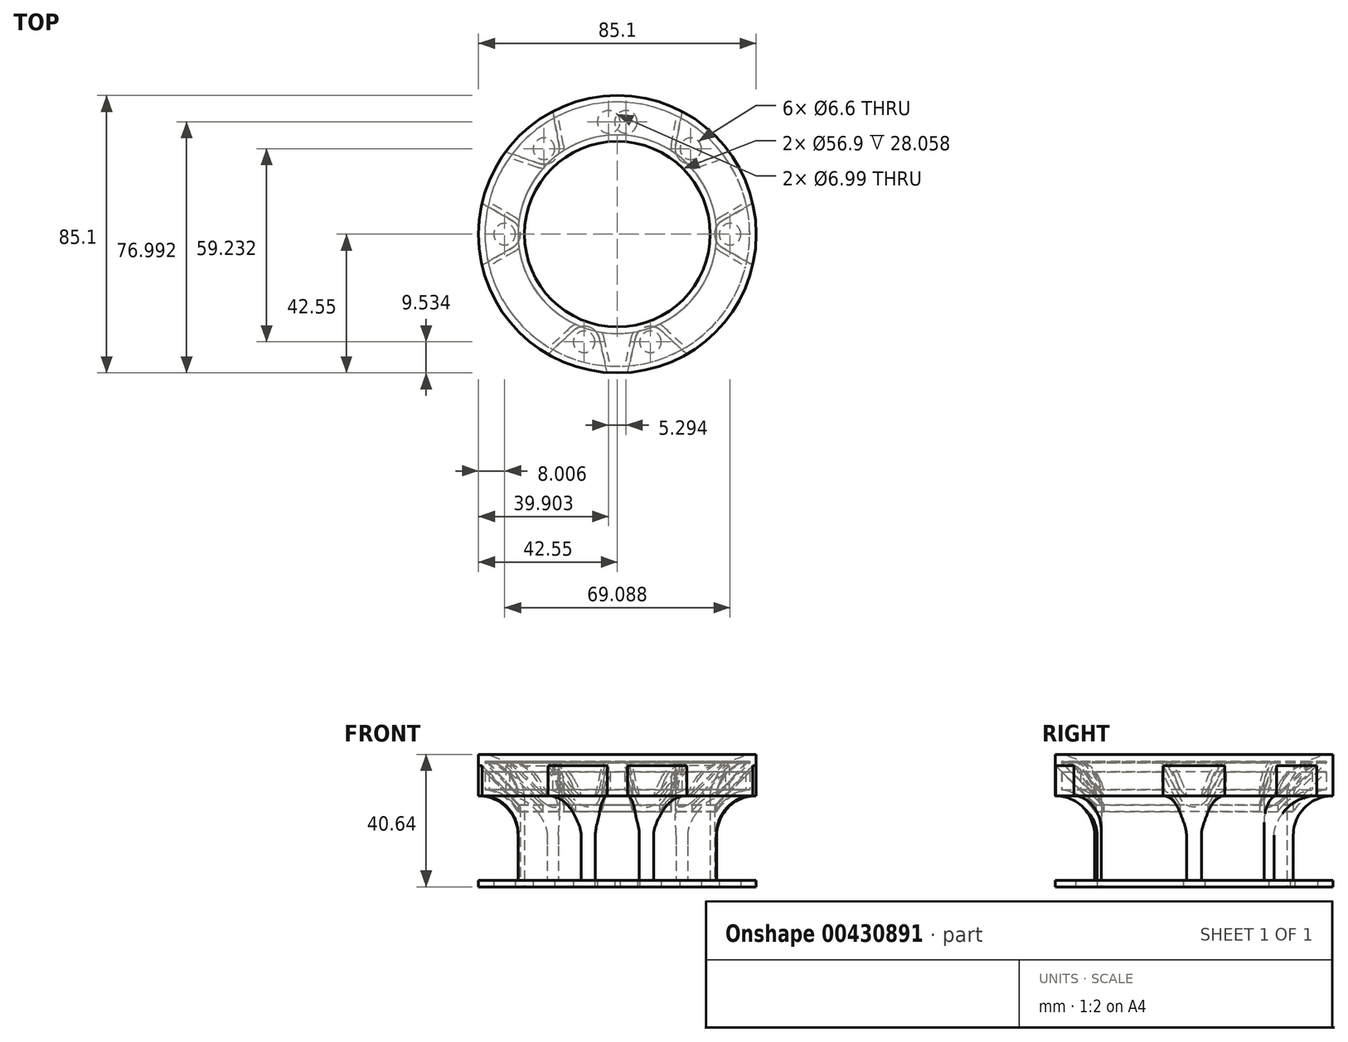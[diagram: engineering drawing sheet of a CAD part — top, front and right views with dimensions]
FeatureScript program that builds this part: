
annotation { "Feature Type Name" : "Feature", "Feature Type Description" : "" }
export const myFeature = defineFeature(function(context is Context, id is Id, definition is map)
    precondition{}
    {
        {
            var Q0;
            Q0=qCreatedBy(makeId("Front.planeOp"),FACE);
            var sketch = newSketch(context, id + "F0", { "sketchPlane" : qUnion([Q0])});
            skLineSegment(sketch, "E0", {"start": v(-42.55, 0) * mm, "end": v(-28.45, 0) * mm});
            skLineSegment(sketch, "E1", {"start": v(-28.45, 0) * mm, "end": v(-28.45, 28.06) * mm});
            skLineSegment(sketch, "E2", {"start": v(-42.55, 40.64) * mm, "end": v(-42.55, 27.94) * mm});
            skArc(sketch, "E3", {"start": v(-42.55, 40.64) * mm, "mid": v(-33.1, 37.04) * mm, "end": v(-28.45, 28.06) * mm});
            skArc(sketch, "E4.0", {"start": v(-40.55, 38.47) * mm, "mid": v(-33.75, 34.89) * mm, "end": v(-30.45, 27.94) * mm});
            skLineSegment(sketch, "E5.0", {"start": v(-42.55, 2) * mm, "end": v(-30.45, 2) * mm});
            skLineSegment(sketch, "E6.0", {"start": v(-30.45, 2) * mm, "end": v(-30.45, 15.84) * mm});
            skLineSegment(sketch, "E7", {"start": v(-42.55, 2) * mm, "end": v(-42.55, 0) * mm});
            skLineSegment(sketch, "E8.trimOffspring", {"start": v(-40.55, 38.47) * mm, "end": v(-40.55, 38.04) * mm});
            skLineSegment(sketch, "E9.trimOffspring", {"start": v(-30.45, 23.08) * mm, "end": v(-30.45, 25.11) * mm});
            skLineSegment(sketch, "E10", {"start": v(-30.45, 27.94) * mm, "end": v(-40.55, 38.04) * mm});
            skLineSegment(sketch, "E11.0", {"start": v(-30.45, 25.11) * mm, "end": v(-40.55, 35.2) * mm});
            skLineSegment(sketch, "E12.trimOffspring", {"start": v(-40.55, 35.2) * mm, "end": v(-40.55, 29.8) * mm});
            skArc(sketch, "E13", {"start": v(-30.45, 15.84) * mm, "mid": v(-34, 24.4) * mm, "end": v(-42.55, 27.94) * mm});
            skArc(sketch, "E14.0", {"start": v(-30.45, 23.08) * mm, "mid": v(-34.74, 27.58) * mm, "end": v(-40.55, 29.8) * mm});
            skSolve(sketch);
        }
        {
            var Q0;
            Q0=qCreatedBy(makeId("Front.planeOp"),FACE);
            var sketch = newSketch(context, id + "F1", { "sketchPlane" : qUnion([Q0])});
            skLineSegment(sketch, "E15", {"start": v(0, 0) * mm, "end": v(0, 53.03) * mm});
            skSolve(sketch);
        }
        {
            var Q0;
            Q0=makeQuery(id+"F0.imprint","IMPRINT",FACE,{"disambiguationData":[TD([[makeQuery(id+"F0.imprint","IMPRINT",EDGE,{"derivedFrom":sQuery(id+"F0.wireOp",EDGE,"E0")}),1.0]])]});
            var Q1;
            Q1=sQuery(id+"F0.wireOp",EDGE,"E2");
            var Q2;
            Q2=sQuery(id+"F0.wireOp",EDGE,"E3");
            var Q3;
            Q3=sQuery(id+"F0.wireOp",EDGE,"E1");
            var Q4;
            Q4=sQuery(id+"F0.wireOp",EDGE,"E0");
            var Q5;
            Q5=sQuery(id+"F1.wireOp",EDGE,"E15");
            revolve(context, id + "F2", {"entities" : qUnion([Q0]), "surfaceEntities" : qUnion([Q1, Q2, Q3, Q4]), "axis" : qUnion([Q5]), "revolveType" : RevolveType.FULL});
        }
        {
            var Q0;
            Q0=qCreatedBy(makeId("Top.planeOp"),FACE);
            var sketch = newSketch(context, id + "F3", { "sketchPlane" : qUnion([Q0])});
            skCircle(sketch, "E16", {"center": v(-34.54, 0) * mm, "radius": 3.3 * mm});
            skCircle(sketch, "E17", {"center": v(-2.65, 34.44) * mm, "radius": 3.5 * mm});
            skCircle(sketch, "E18", {"center": v(10.16, -33.02) * mm, "radius": 3.3 * mm});
            skCircle(sketch, "E19", {"center": v(22.5, 26.22) * mm, "radius": 3.3 * mm});
            skSolve(sketch);
        }
        {
            var Q0;
            Q0 = qSketchRegion(id + "F3", true);
            extrude(context, id + "F4", {"entities" : qUnion([Q0]), "operationType" : NewBodyOperationType.REMOVE, "endBound" : BoundingType.UP_TO_NEXT, "depth" : 4.06 * mm});
        }
        {
            var Q0;
            Q0=makeQuery(id+"F2.opRevolve","SWEPT_FACE",FACE,{"disambiguationData":[OSD([sQuery(id+"F0.wireOp",EDGE,"E5.0")])]});
            var sketch = newSketch(context, id + "F5", { "sketchPlane" : qUnion([Q0])});
            skArc(sketch, "E20", {"start": v(-32.16, -4.12) * mm, "mid": v(-29.78, 0) * mm, "end": v(-32.16, 4.12) * mm});
            skArc(sketch, "E21", {"start": v(17.82, 27.1) * mm, "mid": v(19.4, 22.6) * mm, "end": v(24.08, 21.72) * mm});
            skArc(sketch, "E22", {"start": v(13.4, -29.53) * mm, "mid": v(8.76, -28.46) * mm, "end": v(5.52, -31.95) * mm});
            skLineSegment(sketch, "E23", {"start": v(-32.16, 4.12) * mm, "end": v(-41.47, 9.5) * mm});
            skLineSegment(sketch, "E24", {"start": v(-32.16, -4.12) * mm, "end": v(-41.47, -9.5) * mm});
            skLineSegment(sketch, "E25", {"start": v(13.4, -29.53) * mm, "end": v(21.28, -36.84) * mm});
            skLineSegment(sketch, "E26", {"start": v(5.52, -31.95) * mm, "end": v(3.12, -42.43) * mm});
            skLineSegment(sketch, "E27", {"start": v(17.82, 27.1) * mm, "end": v(19.8, 37.66) * mm});
            skLineSegment(sketch, "E28", {"start": v(24.08, 21.72) * mm, "end": v(34.21, 25.29) * mm});
            skArc(sketch, "E29", {"start": v(-41.47, 9.5) * mm, "mid": v(-42.55, 0) * mm, "end": v(-41.47, -9.5) * mm});
            skArc(sketch, "E30.trimOffspring", {"start": v(34.21, 25.29) * mm, "mid": v(27.7, 32.29) * mm, "end": v(19.8, 37.66) * mm});
            skArc(sketch, "E31.trimOffspring", {"start": v(3.12, -42.43) * mm, "mid": v(12.51, -40.66) * mm, "end": v(21.28, -36.84) * mm});
            skLineSegment(sketch, "E32", {"start": v(-29.78, 0) * mm, "end": v(0, 0) * mm});
            skLineSegment(sketch, "E33", {"start": v(19.4, 22.6) * mm, "end": v(0, 0) * mm});
            skLineSegment(sketch, "E34", {"start": v(0, 0) * mm, "end": v(8.76, -28.46) * mm});
            skSolve(sketch);
        }
        {
            var Q0;
            Q0 = qSketchRegion(id + "F5", true);
            var Q1;
            Q1=makeQuery(id+"F2.opRevolve","SWEPT_FACE",FACE,{"disambiguationData":[OSD([sQuery(id+"F0.wireOp",EDGE,"E11.0")])]});
            var Q2;
            Q2=makeQuery(id+"FeETeO8mRZ9KAlR_1.opThicken","SWEPT_BODY",BODY,{"disambiguationData":[OSD([sQuery(id+"F0.wireOp",EDGE,"E0")])]});
            extrude(context, id + "F6", {"entities" : qUnion([Q0]), "operationType" : NewBodyOperationType.REMOVE, "endBound" : BoundingType.UP_TO_SURFACE, "endBoundEntityFace" : qUnion([Q1]), "endBoundEntityBody" : qUnion([Q2]), "depth" : 22.73 * mm, "offsetDistance" : 25 * mm});
        }
        {
            var Q0;
            Q0=qCreatedBy(makeId("Top.planeOp"),FACE);
            cPlane(context, id + "F7", {"entities" : qUnion([Q0]), "cplaneType" : CPlaneType.OFFSET, "offset" : 30 * mm, "width" : 150 * mm, "height" : 150 * mm});
        }
        {
            var Q0;
            Q0=qCreatedBy(id+"F7.planeOp",FACE);
            var sketch = newSketch(context, id + "F8", { "sketchPlane" : qUnion([Q0])});
            skArc(sketch, "E35", {"start": v(-32.16, -4.12) * mm, "mid": v(-29.78, 0) * mm, "end": v(-32.16, 4.12) * mm});
            skArc(sketch, "E36", {"start": v(17.81, 27.09) * mm, "mid": v(19.4, 22.6) * mm, "end": v(24.08, 21.72) * mm});
            skArc(sketch, "E37", {"start": v(13.4, -29.53) * mm, "mid": v(8.76, -28.46) * mm, "end": v(5.52, -31.95) * mm});
            skArc(sketch, "E38", {"start": v(-41.14, 10.85) * mm, "mid": v(-41.31, 10.17) * mm, "end": v(-41.47, 9.5) * mm});
            skLineSegment(sketch, "E39", {"start": v(-32.16, 4.12) * mm, "end": v(-41.47, 9.5) * mm});
            skLineSegment(sketch, "E40", {"start": v(-32.16, -4.12) * mm, "end": v(-41.47, -9.5) * mm});
            skLineSegment(sketch, "E41", {"start": v(13.4, -29.53) * mm, "end": v(21.28, -36.84) * mm});
            skLineSegment(sketch, "E42", {"start": v(24.08, 21.72) * mm, "end": v(34.21, 25.29) * mm});
            skLineSegment(sketch, "E43", {"start": v(17.81, 27.09) * mm, "end": v(19.8, 37.66) * mm});
            skLineSegment(sketch, "E44", {"start": v(5.52, -31.95) * mm, "end": v(3.12, -42.43) * mm});
            skLineSegment(sketch, "E45.0", {"start": v(-31.5, 5.28) * mm, "end": v(-41.14, 10.85) * mm});
            skArc(sketch, "E46.0", {"start": v(-31.5, -5.28) * mm, "mid": v(-28.45, 0) * mm, "end": v(-31.5, 5.28) * mm});
            skLineSegment(sketch, "E47.0", {"start": v(-31.5, -5.28) * mm, "end": v(-41.14, -10.85) * mm});
            skLineSegment(sketch, "E48.0", {"start": v(16.5, 27.33) * mm, "end": v(18.56, 38.28) * mm});
            skArc(sketch, "E49.0", {"start": v(16.5, 27.33) * mm, "mid": v(18.53, 21.59) * mm, "end": v(24.52, 20.47) * mm});
            skLineSegment(sketch, "E50.0", {"start": v(24.48, 20.45) * mm, "end": v(35.02, 24.16) * mm});
            skLineSegment(sketch, "E51.0", {"start": v(4.22, -31.66) * mm, "end": v(1.74, -42.5) * mm});
            skArc(sketch, "E52.0", {"start": v(14.31, -28.55) * mm, "mid": v(8.37, -27.19) * mm, "end": v(4.22, -31.66) * mm});
            skLineSegment(sketch, "E53.0", {"start": v(14.31, -28.55) * mm, "end": v(22.47, -36.13) * mm});
            skArc(sketch, "E54.trimOffspring", {"start": v(35.02, 24.16) * mm, "mid": v(34.62, 24.73) * mm, "end": v(34.21, 25.29) * mm});
            skArc(sketch, "E55.trimOffspring", {"start": v(1.74, -42.5) * mm, "mid": v(2.43, -42.48) * mm, "end": v(3.12, -42.43) * mm});
            skArc(sketch, "E56.trimOffspring", {"start": v(-41.47, -9.5) * mm, "mid": v(-41.31, -10.17) * mm, "end": v(-41.14, -10.85) * mm});
            skArc(sketch, "E57.trimOffspring", {"start": v(19.8, 37.66) * mm, "mid": v(19.18, 37.98) * mm, "end": v(18.56, 38.28) * mm});
            skArc(sketch, "E58.trimOffspring", {"start": v(21.28, -36.84) * mm, "mid": v(21.88, -36.5) * mm, "end": v(22.47, -36.13) * mm});
            skSolve(sketch);
        }
        {
            var Q0;
            Q0 = qSketchRegion(id + "F8", true);
            extrude(context, id + "F9", {"entities" : qUnion([Q0]), "operationType" : NewBodyOperationType.ADD, "endBound" : BoundingType.SYMMETRIC, "depth" : 35 * mm, "offsetDistance" : 25 * mm});
        }
        {
            var Q0;
            Q0=makeQuery(id+"F9.opExtrude","CAP_FACE",FACE,{"disambiguationData":[OSD([sQuery(id+"F8.wireOp",EDGE,"E36"),sQuery(id+"F8.wireOp",EDGE,"E42"),sQuery(id+"F8.wireOp",EDGE,"E43"),sQuery(id+"F8.wireOp",EDGE,"E48.0"),sQuery(id+"F8.wireOp",EDGE,"E49.0"),sQuery(id+"F8.wireOp",EDGE,"E50.0"),sQuery(id+"F8.wireOp",EDGE,"E54.trimOffspring"),sQuery(id+"F8.wireOp",EDGE,"E57.trimOffspring")])],"isStart":false});
            var Q1;
            Q1=makeQuery(id+"F9.opExtrude","CAP_FACE",FACE,{"disambiguationData":[OSD([sQuery(id+"F8.wireOp",EDGE,"E35"),sQuery(id+"F8.wireOp",EDGE,"E38"),sQuery(id+"F8.wireOp",EDGE,"E39"),sQuery(id+"F8.wireOp",EDGE,"E40"),sQuery(id+"F8.wireOp",EDGE,"E45.0"),sQuery(id+"F8.wireOp",EDGE,"E46.0"),sQuery(id+"F8.wireOp",EDGE,"E47.0"),sQuery(id+"F8.wireOp",EDGE,"E56.trimOffspring")])],"isStart":false});
            var Q2;
            Q2=makeQuery(id+"F9.opExtrude","CAP_FACE",FACE,{"disambiguationData":[OSD([sQuery(id+"F8.wireOp",EDGE,"E37"),sQuery(id+"F8.wireOp",EDGE,"E41"),sQuery(id+"F8.wireOp",EDGE,"E44"),sQuery(id+"F8.wireOp",EDGE,"E51.0"),sQuery(id+"F8.wireOp",EDGE,"E52.0"),sQuery(id+"F8.wireOp",EDGE,"E53.0"),sQuery(id+"F8.wireOp",EDGE,"E55.trimOffspring"),sQuery(id+"F8.wireOp",EDGE,"E58.trimOffspring")])],"isStart":false});
            var Q3;
            Q3=makeQuery(id+"F9.boolean.opBoolean","SPLIT",FACE,{"disambiguationData":[TD([makeQuery(id+"F2.opRevolve","SWEPT_FACE",FACE,{"disambiguationData":[OSD([sQuery(id+"F0.wireOp",EDGE,"E1")])]})])],"derivedFrom":makeQuery(id+"F2.opRevolve","SWEPT_FACE",FACE,{"disambiguationData":[OSD([sQuery(id+"F0.wireOp",EDGE,"E3")])]})});
            extrude(context, id + "F10", {"entities" : qUnion([Q0, Q1, Q2]), "operationType" : NewBodyOperationType.REMOVE, "endBound" : BoundingType.UP_TO_SURFACE, "oppositeDirection" : true, "depth" : 25 * mm, "endBoundEntityFace" : qUnion([Q3]), "offsetDistance" : 25 * mm});
        }
        {
            var Q0;
            {var subQ0=sQuery(id+"F8.wireOp",EDGE,"E52.0");var subQ1=sQuery(id+"F8.wireOp",EDGE,"E51.0");var subQ2=sQuery(id+"F8.wireOp",EDGE,"E44");var subQ3=sQuery(id+"F8.wireOp",EDGE,"E37");var subQ4=sQuery(id+"F8.wireOp",EDGE,"E58.trimOffspring");var subQ5=sQuery(id+"F8.wireOp",EDGE,"E55.trimOffspring");Q0=makeQuery(id+"F9.boolean.opBoolean","SPLIT",FACE,{"disambiguationData":[TD([makeQuery(id+"F6.boolean.opBoolean","COPY",FACE,{"derivedFrom":makeQuery(id+"F6.opExtrude","SWEPT_FACE",FACE,{"disambiguationData":[OSD([sQuery(id+"F5.wireOp",EDGE,"E26")])]})})])],"derivedFrom":makeQuery(id+"F9.opExtrude","CAP_FACE",FACE,{"disambiguationData":[OSD([subQ3,sQuery(id+"F8.wireOp",EDGE,"E41"),subQ2,subQ1,subQ0,sQuery(id+"F8.wireOp",EDGE,"E53.0"),subQ5,subQ4])],"isStart":true})});}
            var Q1;
            {var subQ0=sQuery(id+"F8.wireOp",EDGE,"E37");var subQ1=sQuery(id+"F8.wireOp",EDGE,"E58.trimOffspring");var subQ2=sQuery(id+"F8.wireOp",EDGE,"E53.0");var subQ3=sQuery(id+"F8.wireOp",EDGE,"E52.0");var subQ4=sQuery(id+"F8.wireOp",EDGE,"E41");var subQ5=sQuery(id+"F8.wireOp",EDGE,"E55.trimOffspring");Q1=makeQuery(id+"F9.boolean.opBoolean","SPLIT",FACE,{"disambiguationData":[TD([makeQuery(id+"F6.boolean.opBoolean","COPY",FACE,{"derivedFrom":makeQuery(id+"F6.opExtrude","SWEPT_FACE",FACE,{"disambiguationData":[OSD([sQuery(id+"F5.wireOp",EDGE,"E25")])]})})])],"derivedFrom":makeQuery(id+"F9.opExtrude","CAP_FACE",FACE,{"disambiguationData":[OSD([subQ0,subQ4,sQuery(id+"F8.wireOp",EDGE,"E44"),sQuery(id+"F8.wireOp",EDGE,"E51.0"),subQ3,subQ2,subQ5,subQ1])],"isStart":true})});}
            var Q2;
            {var subQ0=sQuery(id+"F8.wireOp",EDGE,"E50.0");var subQ1=sQuery(id+"F8.wireOp",EDGE,"E54.trimOffspring");var subQ2=sQuery(id+"F8.wireOp",EDGE,"E36");var subQ3=sQuery(id+"F8.wireOp",EDGE,"E49.0");var subQ4=sQuery(id+"F8.wireOp",EDGE,"E42");var subQ5=sQuery(id+"F8.wireOp",EDGE,"E57.trimOffspring");Q2=makeQuery(id+"F9.boolean.opBoolean","SPLIT",FACE,{"disambiguationData":[TD([makeQuery(id+"F6.boolean.opBoolean","COPY",FACE,{"derivedFrom":makeQuery(id+"F6.opExtrude","SWEPT_FACE",FACE,{"disambiguationData":[OSD([sQuery(id+"F5.wireOp",EDGE,"E28")])]})})])],"derivedFrom":makeQuery(id+"F9.opExtrude","CAP_FACE",FACE,{"disambiguationData":[OSD([subQ2,subQ4,sQuery(id+"F8.wireOp",EDGE,"E43"),sQuery(id+"F8.wireOp",EDGE,"E48.0"),subQ3,subQ0,subQ1,subQ5])],"isStart":true})});}
            var Q3;
            {var subQ0=sQuery(id+"F8.wireOp",EDGE,"E49.0");var subQ1=sQuery(id+"F8.wireOp",EDGE,"E54.trimOffspring");var subQ2=sQuery(id+"F8.wireOp",EDGE,"E43");var subQ3=sQuery(id+"F8.wireOp",EDGE,"E36");var subQ4=sQuery(id+"F8.wireOp",EDGE,"E48.0");var subQ5=sQuery(id+"F8.wireOp",EDGE,"E57.trimOffspring");Q3=makeQuery(id+"F9.boolean.opBoolean","SPLIT",FACE,{"disambiguationData":[TD([makeQuery(id+"F6.boolean.opBoolean","COPY",FACE,{"derivedFrom":makeQuery(id+"F6.opExtrude","SWEPT_FACE",FACE,{"disambiguationData":[OSD([sQuery(id+"F5.wireOp",EDGE,"E27")])]})})])],"derivedFrom":makeQuery(id+"F9.opExtrude","CAP_FACE",FACE,{"disambiguationData":[OSD([subQ3,sQuery(id+"F8.wireOp",EDGE,"E42"),subQ2,subQ4,subQ0,sQuery(id+"F8.wireOp",EDGE,"E50.0"),subQ1,subQ5])],"isStart":true})});}
            var Q4;
            {var subQ0=sQuery(id+"F8.wireOp",EDGE,"E46.0");var subQ1=sQuery(id+"F8.wireOp",EDGE,"E45.0");var subQ2=sQuery(id+"F8.wireOp",EDGE,"E35");var subQ3=sQuery(id+"F8.wireOp",EDGE,"E38");var subQ4=sQuery(id+"F8.wireOp",EDGE,"E39");var subQ5=sQuery(id+"F8.wireOp",EDGE,"E56.trimOffspring");Q4=makeQuery(id+"F9.boolean.opBoolean","SPLIT",FACE,{"disambiguationData":[TD([makeQuery(id+"F6.boolean.opBoolean","COPY",FACE,{"derivedFrom":makeQuery(id+"F6.opExtrude","SWEPT_FACE",FACE,{"disambiguationData":[OSD([sQuery(id+"F5.wireOp",EDGE,"E23")])]})})])],"derivedFrom":makeQuery(id+"F9.opExtrude","CAP_FACE",FACE,{"disambiguationData":[OSD([subQ2,subQ3,subQ4,sQuery(id+"F8.wireOp",EDGE,"E40"),subQ1,subQ0,sQuery(id+"F8.wireOp",EDGE,"E47.0"),subQ5])],"isStart":true})});}
            var Q5;
            {var subQ0=sQuery(id+"F8.wireOp",EDGE,"E46.0");var subQ1=sQuery(id+"F8.wireOp",EDGE,"E38");var subQ2=sQuery(id+"F8.wireOp",EDGE,"E47.0");var subQ3=sQuery(id+"F8.wireOp",EDGE,"E40");var subQ4=sQuery(id+"F8.wireOp",EDGE,"E35");var subQ5=sQuery(id+"F8.wireOp",EDGE,"E56.trimOffspring");Q5=makeQuery(id+"F9.boolean.opBoolean","SPLIT",FACE,{"disambiguationData":[TD([makeQuery(id+"F6.boolean.opBoolean","COPY",FACE,{"derivedFrom":makeQuery(id+"F6.opExtrude","SWEPT_FACE",FACE,{"disambiguationData":[OSD([sQuery(id+"F5.wireOp",EDGE,"E24")])]})})])],"derivedFrom":makeQuery(id+"F9.opExtrude","CAP_FACE",FACE,{"disambiguationData":[OSD([subQ4,subQ1,sQuery(id+"F8.wireOp",EDGE,"E39"),subQ3,sQuery(id+"F8.wireOp",EDGE,"E45.0"),subQ0,subQ2,subQ5])],"isStart":true})});}
            var Q6;
            Q6=makeQuery(id+"F6.boolean.opBoolean","SPLIT",FACE,{"disambiguationData":[TD([makeQuery(id+"F6.opExtrude","SWEPT_FACE",FACE,{"disambiguationData":[OSD([sQuery(id+"F5.wireOp",EDGE,"E25")])]})])],"derivedFrom":makeQuery(id+"F2.opRevolve","SWEPT_FACE",FACE,{"disambiguationData":[OSD([sQuery(id+"F0.wireOp",EDGE,"E13")])]})});
            extrude(context, id + "F11", {"entities" : qUnion([Q0, Q1, Q2, Q3, Q4, Q5]), "operationType" : NewBodyOperationType.REMOVE, "endBound" : BoundingType.UP_TO_SURFACE, "oppositeDirection" : true, "depth" : 25 * mm, "endBoundEntityFace" : qUnion([Q6]), "offsetDistance" : 25 * mm});
        }
        {
            var Q0;
            Q0=makeQuery(id+"F2.opRevolve","SWEPT_BODY",BODY,{"disambiguationData":[OSD([sQuery(id+"F0.wireOp",EDGE,"E0"),sQuery(id+"F0.wireOp",EDGE,"E1"),sQuery(id+"F0.wireOp",EDGE,"E2"),sQuery(id+"F0.wireOp",EDGE,"E3"),sQuery(id+"F0.wireOp",EDGE,"E4.0"),sQuery(id+"F0.wireOp",EDGE,"E5.0"),sQuery(id+"F0.wireOp",EDGE,"E6.0"),sQuery(id+"F0.wireOp",EDGE,"E7"),sQuery(id+"F0.wireOp",EDGE,"E8.trimOffspring"),sQuery(id+"F0.wireOp",EDGE,"E9.trimOffspring"),sQuery(id+"F0.wireOp",EDGE,"E10"),sQuery(id+"F0.wireOp",EDGE,"E11.0"),sQuery(id+"F0.wireOp",EDGE,"E12.trimOffspring"),sQuery(id+"F0.wireOp",EDGE,"E13"),sQuery(id+"F0.wireOp",EDGE,"E14.0")])]});
            var Q1;
            Q1=qCreatedBy(makeId("Right.planeOp"),FACE);
            mirror(context, id + "F12", {"entities" : qUnion([Q0]), "mirrorPlane" : qUnion([Q1])});
        }
    });
